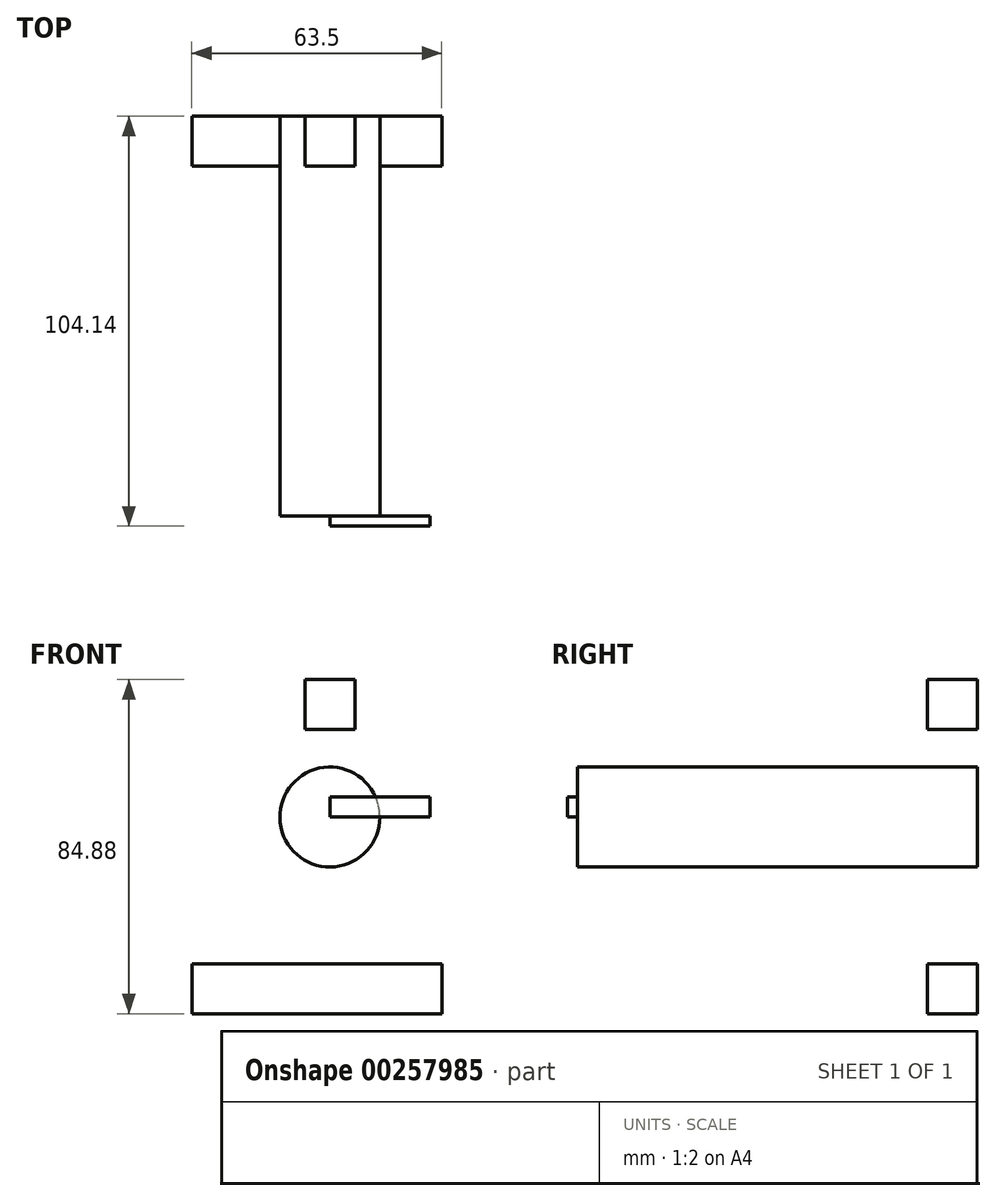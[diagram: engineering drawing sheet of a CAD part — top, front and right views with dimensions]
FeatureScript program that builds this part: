
annotation { "Feature Type Name" : "Feature", "Feature Type Description" : "" }
export const myFeature = defineFeature(function(context is Context, id is Id, definition is map)
    precondition{}
    {
        {
            var Q0;
            Q0=qCreatedBy(makeId("Front.planeOp"),FACE);
            var sketch = newSketch(context, id + "F0", { "sketchPlane" : qUnion([Q0])});
            skCircle(sketch, "E0", {"center": v(0, 0) * mm, "radius": 12.7 * mm});
            skSolve(sketch);
        }
        {
            var Q0;
            Q0=qSketchRegion(id+"F0",true);
            extrude(context, id + "F1", {"entities" : qUnion([Q0]), "depth" : 101.6 * mm});
        }
        {
            var Q0;
            Q0=qCreatedBy(makeId("Front.planeOp"),FACE);
            var sketch = newSketch(context, id + "F2", { "sketchPlane" : qUnion([Q0])});
            skLineSegment(sketch, "E1.bottom", {"start": v(28.44, -37.26) * mm, "end": v(-35.06, -37.26) * mm});
            skLineSegment(sketch, "E1.top", {"start": v(28.44, -49.96) * mm, "end": v(-35.06, -49.96) * mm});
            skLineSegment(sketch, "E1.left", {"start": v(28.44, -37.26) * mm, "end": v(28.44, -49.96) * mm});
            skLineSegment(sketch, "E1.right", {"start": v(-35.06, -37.26) * mm, "end": v(-35.06, -49.96) * mm});
            skSolve(sketch);
        }
        {
            var Q0;
            Q0=qSketchRegion(id+"F2",true);
            extrude(context, id + "F3", {"entities" : qUnion([Q0]), "depth" : 12.7 * mm});
        }
        {
            var Q0;
            Q0=makeQuery(id+"F1.opExtrude","CAP_FACE",FACE,{"disambiguationData":[OSD([sQuery(id+"F0.wireOp",EDGE,"E0")])],"isStart":false});
            var sketch = newSketch(context, id + "F4", { "sketchPlane" : qUnion([Q0])});
            skLineSegment(sketch, "E2.bottom", {"start": v(0, 0) * mm, "end": v(25.4, 0) * mm});
            skLineSegment(sketch, "E2.top", {"start": v(0, 5.08) * mm, "end": v(25.4, 5.08) * mm});
            skLineSegment(sketch, "E2.left", {"start": v(0, 0) * mm, "end": v(0, 5.08) * mm});
            skLineSegment(sketch, "E2.right", {"start": v(25.4, 0) * mm, "end": v(25.4, 5.08) * mm});
            skSolve(sketch);
        }
        {
            var Q0;
            {var subQ0=sQuery(id+"F4.wireOp",EDGE,"E2.right");Q0=makeQuery(id+"F4.imprint","IMPRINT",FACE,{"disambiguationData":[TD([[makeQuery(id+"F4.imprint","IMPRINT",EDGE,{"derivedFrom":subQ0}),1.0]])]});}
            var Q1;
            {var subQ0=sQuery(id+"F4.wireOp",EDGE,"E2.left");Q1=makeQuery(id+"F4.imprint","IMPRINT",FACE,{"disambiguationData":[TD([[makeQuery(id+"F4.imprint","IMPRINT",EDGE,{"derivedFrom":subQ0}),-1.0]])]});}
            extrude(context, id + "F5", {"entities" : qUnion([Q0, Q1]), "operationType" : NewBodyOperationType.ADD, "depth" : 2.54 * mm});
        }
        {
            var Q0;
            Q0=qCreatedBy(makeId("Front.planeOp"),FACE);
            var sketch = newSketch(context, id + "F6", { "sketchPlane" : qUnion([Q0])});
            skLineSegment(sketch, "E3.bottom", {"start": v(6.35, 34.92) * mm, "end": v(-6.35, 34.92) * mm});
            skLineSegment(sketch, "E3.top", {"start": v(6.35, 22.22) * mm, "end": v(-6.35, 22.22) * mm});
            skLineSegment(sketch, "E3.left", {"start": v(6.35, 34.92) * mm, "end": v(6.35, 22.22) * mm});
            skLineSegment(sketch, "E3.right", {"start": v(-6.35, 34.92) * mm, "end": v(-6.35, 22.22) * mm});
            skPoint(sketch, "E3.middle", {"position": v(0, 28.57) * mm});
            skSolve(sketch);
        }
        {
            var Q0;
            Q0=qSketchRegion(id+"F6",true);
            extrude(context, id + "F7", {"entities" : qUnion([Q0]), "depth" : 12.7 * mm});
        }
    });
